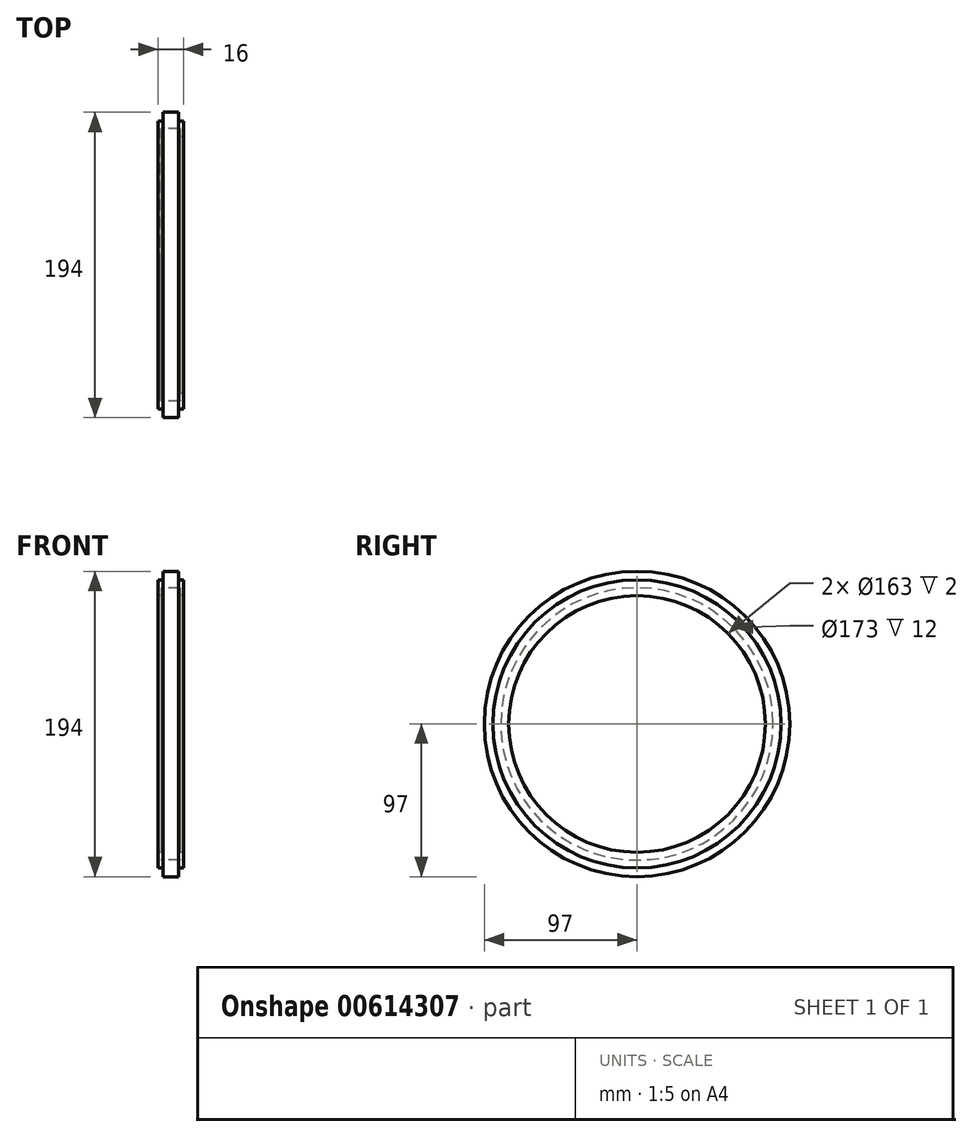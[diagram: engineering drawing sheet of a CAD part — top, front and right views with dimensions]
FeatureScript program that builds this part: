
annotation { "Feature Type Name" : "Feature", "Feature Type Description" : "" }
export const myFeature = defineFeature(function(context is Context, id is Id, definition is map)
    precondition{}
    {
        {
            var Q0;
            Q0=qCreatedBy(makeId("Front.planeOp"),FACE);
            var sketch = newSketch(context, id + "F0", { "sketchPlane" : qUnion([Q0])});
            skLineSegment(sketch, "E0", {"start": v(-8, 91.5) * mm, "end": v(-5, 91.5) * mm});
            skLineSegment(sketch, "E1", {"start": v(-5, 91.5) * mm, "end": v(-5, 97) * mm});
            skLineSegment(sketch, "E2", {"start": v(-5, 97) * mm, "end": v(0, 97) * mm});
            skLineSegment(sketch, "E3", {"start": v(-8, 91.5) * mm, "end": v(-8, 81.5) * mm});
            skLineSegment(sketch, "E4", {"start": v(-8, 81.5) * mm, "end": v(-6, 81.5) * mm});
            skLineSegment(sketch, "E5.MirrorCS", {"start": v(8, 91.5) * mm, "end": v(5, 91.5) * mm});
            skLineSegment(sketch, "E6.MirrorCS", {"start": v(5, 91.5) * mm, "end": v(5, 97) * mm});
            skLineSegment(sketch, "E7.MirrorCS", {"start": v(8, 91.5) * mm, "end": v(8, 81.5) * mm});
            skLineSegment(sketch, "E8.MirrorCS", {"start": v(5, 97) * mm, "end": v(0, 97) * mm});
            skLineSegment(sketch, "E9", {"start": v(-44.78, 0) * mm, "end": v(57.37, 0) * mm, "construction": true});
            skLineSegment(sketch, "E10", {"start": v(-6, 81.5) * mm, "end": v(-6, 86.5) * mm});
            skLineSegment(sketch, "E11", {"start": v(-6, 86.5) * mm, "end": v(0, 86.5) * mm});
            skLineSegment(sketch, "E12.MirrorCS", {"start": v(8, 81.5) * mm, "end": v(6, 81.5) * mm});
            skLineSegment(sketch, "E13.MirrorCS", {"start": v(6, 86.5) * mm, "end": v(0, 86.5) * mm});
            skLineSegment(sketch, "E14.MirrorCS", {"start": v(6, 81.5) * mm, "end": v(6, 86.5) * mm});
            skSolve(sketch);
        }
        {
            var Q0;
            Q0 = qSketchRegion(id + "F0", true);
            var Q1;
            Q1=sQuery(id+"F0.wireOp",EDGE,"E9");
            revolve(context, id + "F1", {"entities" : qUnion([Q0]), "axis" : qUnion([Q1]), "revolveType" : RevolveType.FULL});
        }
    });
